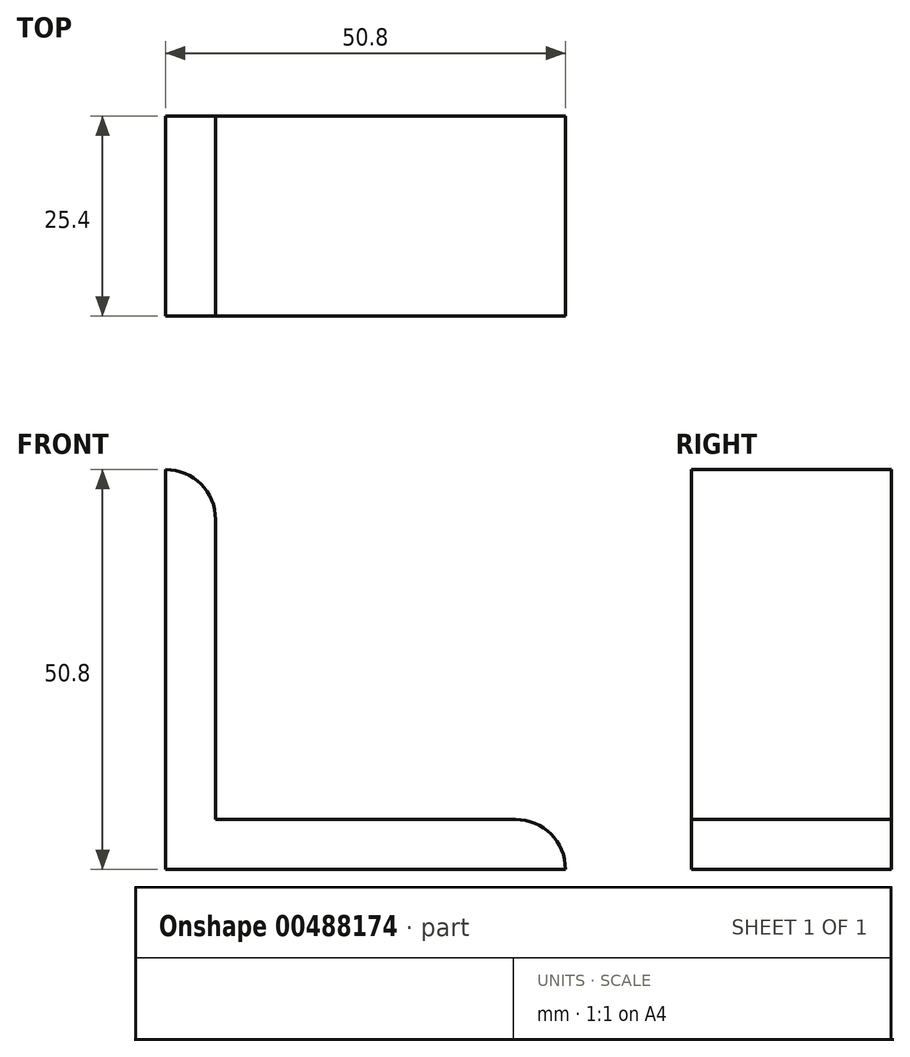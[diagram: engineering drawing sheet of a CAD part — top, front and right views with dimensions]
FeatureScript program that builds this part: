
annotation { "Feature Type Name" : "Feature", "Feature Type Description" : "" }
export const myFeature = defineFeature(function(context is Context, id is Id, definition is map)
    precondition{}
    {
        {
            var Q0;
            Q0=qCreatedBy(makeId("Front.planeOp"),FACE);
            var sketch = newSketch(context, id + "F0", { "sketchPlane" : qUnion([Q0])});
            skLineSegment(sketch, "E0", {"start": v(0, 0) * mm, "end": v(0, 50.8) * mm});
            skLineSegment(sketch, "E1", {"start": v(0, 0) * mm, "end": v(50.8, 0) * mm});
            skLineSegment(sketch, "E2", {"start": v(0, 50.8) * mm, "end": v(0, 50.8) * mm});
            skLineSegment(sketch, "E3", {"start": v(50.8, 0) * mm, "end": v(50.8, 0) * mm});
            skLineSegment(sketch, "E4", {"start": v(44.45, 6.35) * mm, "end": v(6.35, 6.35) * mm});
            skLineSegment(sketch, "E5", {"start": v(6.35, 44.45) * mm, "end": v(6.35, 6.35) * mm});
            skPoint(sketch, "E6.visualSharp", {"position": v(6.35, 50.8) * mm});
            skArc(sketch, "E6.filletArc", {"start": v(6.35, 44.45) * mm, "mid": v(4.5, 48.94) * mm, "end": v(0, 50.8) * mm});
            skPoint(sketch, "E7.visualSharp", {"position": v(50.8, 6.35) * mm});
            skArc(sketch, "E7.filletArc", {"start": v(50.8, 0) * mm, "mid": v(48.94, 4.5) * mm, "end": v(44.45, 6.35) * mm});
            skSolve(sketch);
        }
        {
            var Q0;
            Q0=makeQuery(id+"F0.imprint","IMPRINT",FACE,{"disambiguationData":[TD([[makeQuery(id+"F0.imprint","IMPRINT",EDGE,{"derivedFrom":sQuery(id+"F0.wireOp",EDGE,"E0")}),-1.0]])]});
            extrude(context, id + "F1", {"entities" : qUnion([Q0]), "depth" : 25.4 * mm});
        }
    });
